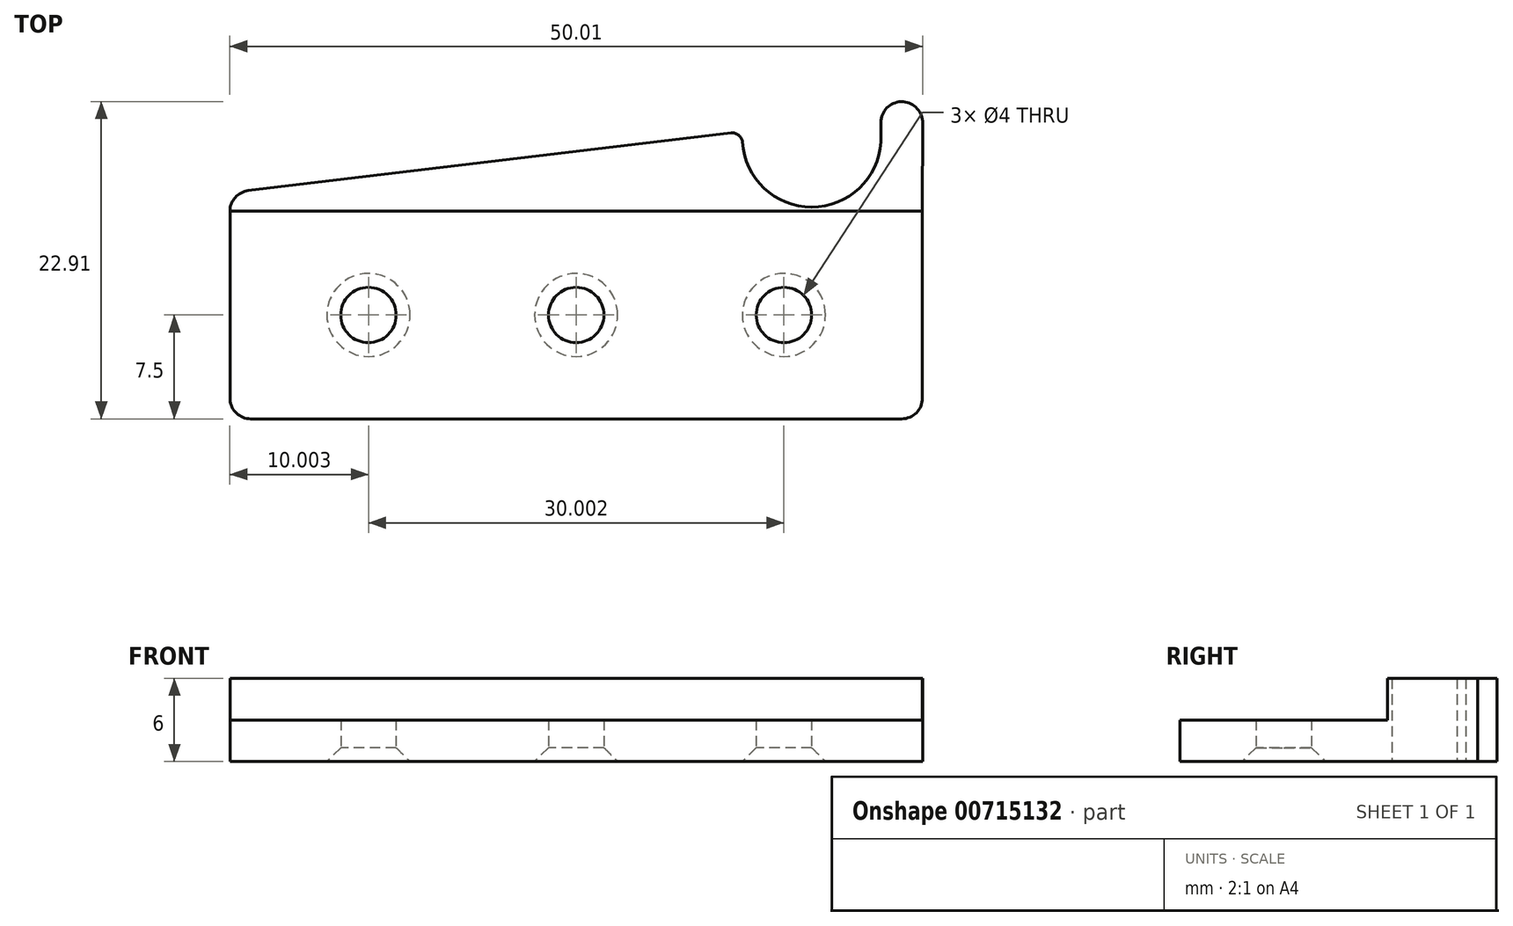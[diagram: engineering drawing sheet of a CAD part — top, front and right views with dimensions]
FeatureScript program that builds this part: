
annotation { "Feature Type Name" : "Feature", "Feature Type Description" : "" }
export const myFeature = defineFeature(function(context is Context, id is Id, definition is map)
    precondition{}
    {
        {
            var Q0;
            Q0=qCreatedBy(makeId("Top.planeOp"),FACE);
            var sketch = newSketch(context, id + "F0", { "sketchPlane" : qUnion([Q0])});
            skLineSegment(sketch, "E0", {"start": v(17.15, 13.15) * mm, "end": v(-17.7, 8.98) * mm});
            skPoint(sketch, "E1.visualSharp", {"position": v(30.99, 15.08) * mm});
            skArc(sketch, "E1.filletArc", {"start": v(30.99, 14) * mm, "mid": v(29.45, 15.4) * mm, "end": v(28, 13.9) * mm});
            skPoint(sketch, "E2.visualSharp", {"position": v(-19.02, 8.82) * mm});
            skArc(sketch, "E2.filletArc", {"start": v(-17.7, 8.98) * mm, "mid": v(-18.64, 8.5) * mm, "end": v(-19.02, 7.5) * mm});
            skCircle(sketch, "E3", {"center": v(-9.02, 0) * mm, "radius": 2 * mm});
            skCircle(sketch, "E4", {"center": v(5.98, 0) * mm, "radius": 2 * mm});
            skCircle(sketch, "E5", {"center": v(20.99, 0) * mm, "radius": 2 * mm});
            skLineSegment(sketch, "E6", {"start": v(-17.52, -7.5) * mm, "end": v(29.48, -7.5) * mm});
            skLineSegment(sketch, "E7", {"start": v(-19.02, 7.5) * mm, "end": v(-19.02, -6) * mm});
            skLineSegment(sketch, "E8", {"start": v(30.99, 14) * mm, "end": v(30.98, -6) * mm});
            skPoint(sketch, "E9.visualSharp", {"position": v(-19.02, -7.5) * mm});
            skArc(sketch, "E9.filletArc", {"start": v(-19.02, -6) * mm, "mid": v(-18.58, -7.06) * mm, "end": v(-17.52, -7.5) * mm});
            skPoint(sketch, "E10.visualSharp", {"position": v(30.98, -7.5) * mm});
            skArc(sketch, "E10.filletArc", {"start": v(29.48, -7.5) * mm, "mid": v(30.54, -7.06) * mm, "end": v(30.98, -6) * mm});
            skLineSegment(sketch, "E11.top", {"start": v(23, 7.8) * mm, "end": v(22.98, 7.8) * mm});
            skPoint(sketch, "E11.middle", {"position": v(23, 12.5) * mm});
            skPoint(sketch, "E12.visualSharp", {"position": v(28, 7.8) * mm});
            skArc(sketch, "E12.filletArc", {"start": v(23, 7.8) * mm, "mid": v(26.43, 9.16) * mm, "end": v(28, 12.5) * mm});
            skPoint(sketch, "E13.visualSharp", {"position": v(18, 7.8) * mm});
            skArc(sketch, "E13.filletArc", {"start": v(18, 12.5) * mm, "mid": v(19.55, 9.16) * mm, "end": v(22.98, 7.8) * mm});
            skLineSegment(sketch, "E14", {"start": v(28, 12.5) * mm, "end": v(28, 13.9) * mm});
            skArc(sketch, "E15", {"start": v(18, 12.5) * mm, "mid": v(17.7, 13) * mm, "end": v(17.15, 13.15) * mm});
            skSolve(sketch);
        }
        {
            var Q0;
            Q0=makeQuery(id+"F0.imprint","IMPRINT",FACE,{"disambiguationData":[TD([[makeQuery(id+"F0.imprint","IMPRINT",EDGE,{"derivedFrom":sQuery(id+"F0.wireOp",EDGE,"E0")}),1.0]])]});
            extrude(context, id + "F1", {"entities" : qUnion([Q0]), "depth" : 6 * mm, "offsetDistance" : 25 * mm});
        }
        {
            var Q0;
            Q0=makeQuery(id+"F1.opExtrude","CAP_FACE",FACE,{"disambiguationData":[OSD([sQuery(id+"F0.wireOp",EDGE,"E0"),sQuery(id+"F0.wireOp",EDGE,"E1.filletArc"),sQuery(id+"F0.wireOp",EDGE,"hq2jynzI-qOXY-DgBt-ycIl-3MHwiE10WQrn"),sQuery(id+"F0.wireOp",EDGE,"1XK0Ufz3-3CLm-33pp-AwrA-GDddTX6uqX9W"),sQuery(id+"F0.wireOp",EDGE,"0376a41d-873c-4e72-b134-8be52620d9e4.filletArc"),sQuery(id+"F0.wireOp",EDGE,"E2.filletArc"),sQuery(id+"F0.wireOp",EDGE,"E3"),sQuery(id+"F0.wireOp",EDGE,"E4"),sQuery(id+"F0.wireOp",EDGE,"E5"),sQuery(id+"F0.wireOp",EDGE,"E6"),sQuery(id+"F0.wireOp",EDGE,"E7"),sQuery(id+"F0.wireOp",EDGE,"E8"),sQuery(id+"F0.wireOp",EDGE,"E9.filletArc"),sQuery(id+"F0.wireOp",EDGE,"E10.filletArc")])],"isStart":false});
            var sketch = newSketch(context, id + "F2", { "sketchPlane" : qUnion([Q0])});
            skLineSegment(sketch, "E16.bottom", {"start": v(-19.01, -7.5) * mm, "end": v(30.99, -7.5) * mm});
            skLineSegment(sketch, "E16.top", {"start": v(-19.01, 7.5) * mm, "end": v(30.99, 7.5) * mm});
            skLineSegment(sketch, "E16.left", {"start": v(-19.01, -7.5) * mm, "end": v(-19.01, 7.5) * mm});
            skLineSegment(sketch, "E16.right", {"start": v(30.99, -7.5) * mm, "end": v(30.99, 7.5) * mm});
            skSolve(sketch);
        }
        {
            var Q0;
            Q0 = qSketchRegion(id + "F2", true);
            extrude(context, id + "F3", {"entities" : qUnion([Q0]), "operationType" : NewBodyOperationType.REMOVE, "oppositeDirection" : true, "depth" : 3 * mm, "offsetDistance" : 25 * mm});
        }
        {
            var Q0;
            Q0=makeQuery(id+"F1.opExtrude","CAP_EDGE",EDGE,{"disambiguationData":[OSD([sQuery(id+"F0.wireOp",EDGE,"E5")])],"isStart":true});
            var Q1;
            Q1=makeQuery(id+"F1.opExtrude","CAP_EDGE",EDGE,{"disambiguationData":[OSD([sQuery(id+"F0.wireOp",EDGE,"E3")])],"isStart":true});
            var Q2;
            Q2=makeQuery(id+"F1.opExtrude","CAP_EDGE",EDGE,{"disambiguationData":[OSD([sQuery(id+"F0.wireOp",EDGE,"E4")])],"isStart":true});
            chamfer(context, id + "F4", {"entities" : qUnion([Q0, Q1, Q2]), "width" : 1 * mm, "tangentPropagation" : true});
        }
    });
